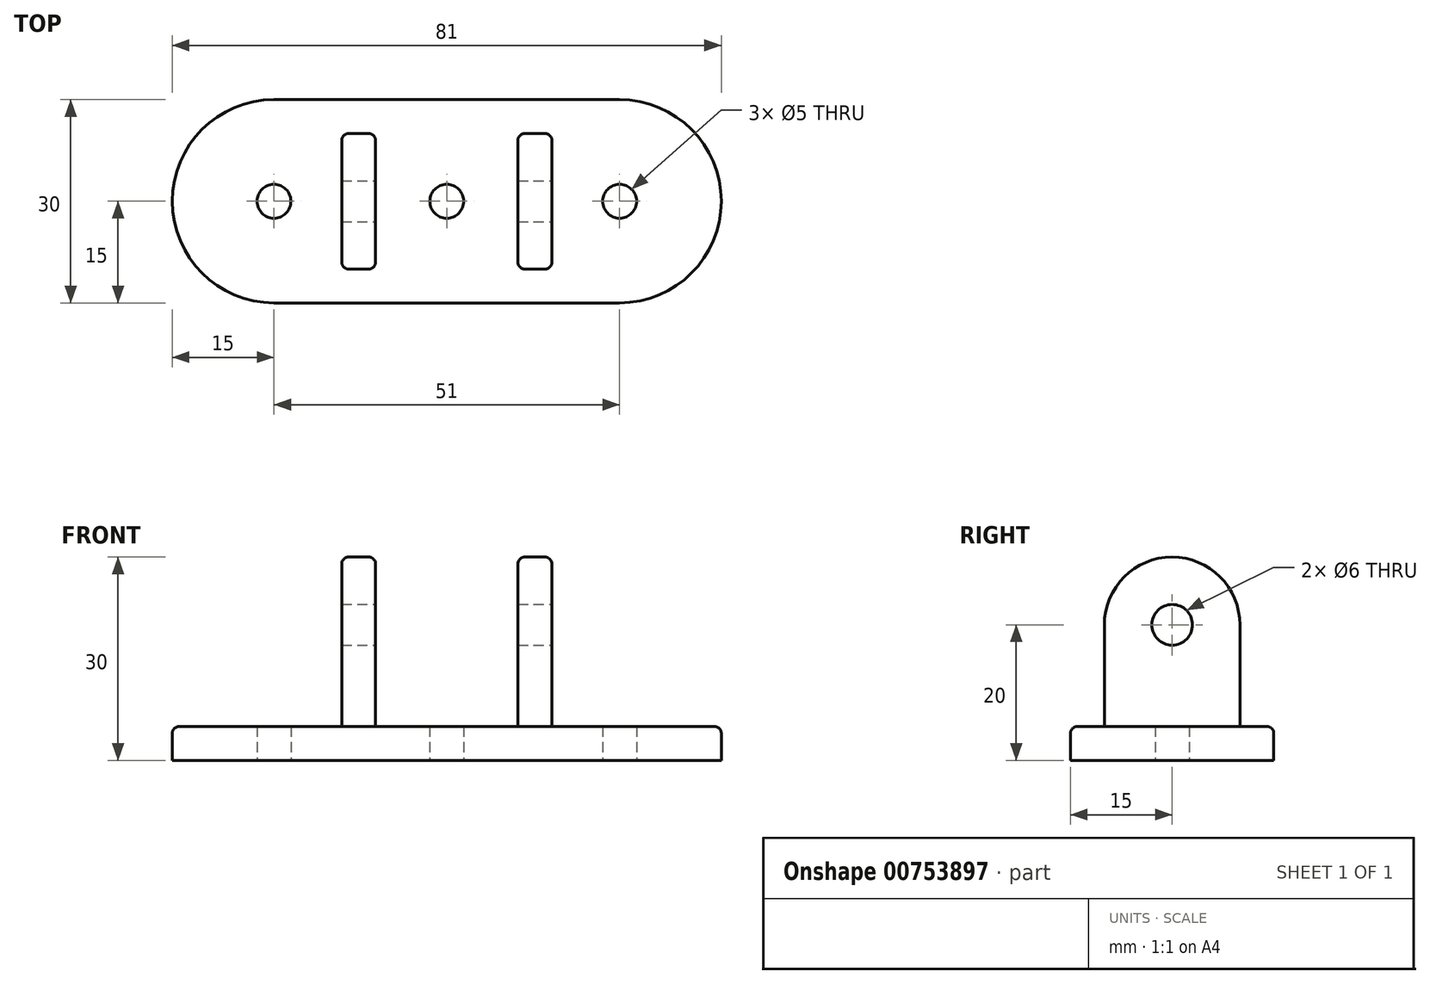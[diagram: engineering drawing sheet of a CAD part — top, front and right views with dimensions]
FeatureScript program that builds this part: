
annotation { "Feature Type Name" : "Feature", "Feature Type Description" : "" }
export const myFeature = defineFeature(function(context is Context, id is Id, definition is map)
    precondition{}
    {
        {
            var Q0;
            Q0=qCreatedBy(makeId("Top.planeOp"),FACE);
            var sketch = newSketch(context, id + "F0", { "sketchPlane" : qUnion([Q0])});
            skLineSegment(sketch, "E0", {"start": v(-0.06, 23.44) * mm, "end": v(-0.06, -19.85) * mm, "construction": true});
            skLineSegment(sketch, "E1.bottom", {"start": v(-25.5, -15) * mm, "end": v(25.5, -15) * mm});
            skLineSegment(sketch, "E1.top", {"start": v(-25.5, 15) * mm, "end": v(25.5, 15) * mm});
            skLineSegment(sketch, "E1.left", {"start": v(-25.5, -15) * mm, "end": v(-25.5, 15) * mm});
            skLineSegment(sketch, "E1.right", {"start": v(25.5, -15) * mm, "end": v(25.5, 15) * mm});
            skPoint(sketch, "E1.middle", {"position": v(0, 0) * mm});
            skCircle(sketch, "E2", {"center": v(-25.5, 0) * mm, "radius": 15 * mm});
            skCircle(sketch, "E3", {"center": v(25.5, 0) * mm, "radius": 15 * mm});
            skCircle(sketch, "E4", {"center": v(-25.5, 0) * mm, "radius": 2.5 * mm});
            skCircle(sketch, "E5", {"center": v(25.5, 0) * mm, "radius": 2.5 * mm});
            skCircle(sketch, "E6", {"center": v(0, 0) * mm, "radius": 2.5 * mm});
            skSolve(sketch);
        }
        {
            var Q0;
            Q0 = qSketchRegion(id + "F0", true);
            extrude(context, id + "F1", {"entities" : qUnion([Q0]), "depth" : 5 * mm, "offsetDistance" : 25 * mm});
        }
        {
            var Q0;
            Q0=makeQuery(id+"F1.opExtrude","CAP_FACE",FACE,{"disambiguationData":[OSD([sQuery(id+"F0.wireOp",EDGE,"E1.bottom"),sQuery(id+"F0.wireOp",EDGE,"E1.top"),sQuery(id+"F0.wireOp",EDGE,"E2"),sQuery(id+"F0.wireOp",EDGE,"E3"),sQuery(id+"F0.wireOp",EDGE,"khoQNaXH-vrLh-hDA5-w1uk-dnxeg6mnAbA2"),sQuery(id+"F0.wireOp",EDGE,"SrZ0nGfz-5AU4-rjPK-6jrb-PTzUXWZE5eXR")])],"isStart":false});
            var sketch = newSketch(context, id + "F2", { "sketchPlane" : qUnion([Q0])});
            skLineSegment(sketch, "E7.bottom", {"start": v(-10.5, -10) * mm, "end": v(-15.5, -10) * mm});
            skLineSegment(sketch, "E7.top", {"start": v(-10.5, 10) * mm, "end": v(-15.5, 10) * mm});
            skLineSegment(sketch, "E7.left", {"start": v(-10.5, -10) * mm, "end": v(-10.5, 10) * mm});
            skLineSegment(sketch, "E7.right", {"start": v(-15.5, -10) * mm, "end": v(-15.5, 10) * mm});
            skPoint(sketch, "E7.middle", {"position": v(-13, 0) * mm});
            skLineSegment(sketch, "E8.bottom", {"start": v(15.5, -10) * mm, "end": v(10.5, -10) * mm});
            skLineSegment(sketch, "E8.top", {"start": v(15.5, 10) * mm, "end": v(10.5, 10) * mm});
            skLineSegment(sketch, "E8.left", {"start": v(15.5, -10) * mm, "end": v(15.5, 10) * mm});
            skLineSegment(sketch, "E8.right", {"start": v(10.5, -10) * mm, "end": v(10.5, 10) * mm});
            skPoint(sketch, "E8.middle", {"position": v(13, 0) * mm});
            skSolve(sketch);
        }
        {
            var Q0;
            Q0=makeQuery(id+"F2.imprint","IMPRINT",FACE,{"disambiguationData":[TD([[makeQuery(id+"F2.imprint","IMPRINT",EDGE,{"derivedFrom":sQuery(id+"F2.wireOp",EDGE,"E8.bottom")}),-1.0]])]});
            extrude(context, id + "F3", {"entities" : qUnion([Q0]), "operationType" : NewBodyOperationType.ADD, "depth" : 15 * mm, "offsetDistance" : 25 * mm});
        }
        {
            var Q0;
            Q0=makeQuery(id+"F2.imprint","IMPRINT",FACE,{"disambiguationData":[TD([[makeQuery(id+"F2.imprint","IMPRINT",EDGE,{"derivedFrom":sQuery(id+"F2.wireOp",EDGE,"E7.bottom")}),-1.0]])]});
            extrude(context, id + "F4", {"entities" : qUnion([Q0]), "operationType" : NewBodyOperationType.ADD, "depth" : 15 * mm, "offsetDistance" : 25 * mm});
        }
        {
            var Q0;
            Q0=makeQuery(id+"F4.opExtrude","SWEPT_FACE",FACE,{"disambiguationData":[OSD([sQuery(id+"F2.wireOp",EDGE,"E7.left")])]});
            var sketch = newSketch(context, id + "F5", { "sketchPlane" : qUnion([Q0])});
            skCircle(sketch, "E9", {"center": v(0, 20) * mm, "radius": 10 * mm});
            skCircle(sketch, "E10", {"center": v(0, 20) * mm, "radius": 3 * mm});
            skSolve(sketch);
        }
        {
            var Q0;
            Q0 = qSketchRegion(id + "F5", true);
            extrude(context, id + "F6", {"entities" : qUnion([Q0]), "operationType" : NewBodyOperationType.ADD, "depth" : -5 * mm, "offsetDistance" : 25 * mm});
        }
        {
            var Q0;
            {var subQ0=sQuery(id+"F5.wireOp",EDGE,"E10");var subQ1=makeQuery(id+"F4.opExtrude","CAP_EDGE",EDGE,{"disambiguationData":[OSD([sQuery(id+"F2.wireOp",EDGE,"E7.left")])],"isStart":false});var subQ2=makeQuery(id+"F5.imprint","INTERSECT",VERTEX,{"disambiguationData":[OD(0.0)],"derivedFrom":[subQ1,subQ0]});Q0=makeQuery(id+"F5.imprint","IMPRINT",FACE,{"disambiguationData":[TD([[makeQuery(id+"F5.imprint","IMPRINT",EDGE,{"disambiguationData":[TD([[subQ2,-1.0]])],"derivedFrom":subQ0}),1.0]])]});}
            extrude(context, id + "F7", {"entities" : qUnion([Q0]), "operationType" : NewBodyOperationType.REMOVE, "oppositeDirection" : true, "depth" : 5 * mm, "offsetDistance" : 25 * mm});
        }
        {
            var Q0;
            Q0=makeQuery(id+"F3.opExtrude","SWEPT_FACE",FACE,{"disambiguationData":[OSD([sQuery(id+"F2.wireOp",EDGE,"E8.left")])]});
            var sketch = newSketch(context, id + "F8", { "sketchPlane" : qUnion([Q0])});
            skCircle(sketch, "E11", {"center": v(0, 20) * mm, "radius": 10 * mm});
            skCircle(sketch, "E12", {"center": v(0, 20) * mm, "radius": 3 * mm});
            skSolve(sketch);
        }
        {
            var Q0;
            Q0 = qSketchRegion(id + "F8", true);
            extrude(context, id + "F9", {"entities" : qUnion([Q0]), "operationType" : NewBodyOperationType.ADD, "depth" : -5 * mm, "offsetDistance" : 25 * mm});
        }
        {
            var Q0;
            {var subQ0=sQuery(id+"F8.wireOp",EDGE,"E12");var subQ1=makeQuery(id+"F3.opExtrude","CAP_EDGE",EDGE,{"disambiguationData":[OSD([sQuery(id+"F2.wireOp",EDGE,"E8.left")])],"isStart":false});var subQ2=makeQuery(id+"F8.imprint","INTERSECT",VERTEX,{"disambiguationData":[OD(0.0)],"derivedFrom":[subQ1,subQ0]});Q0=makeQuery(id+"F8.imprint","IMPRINT",FACE,{"disambiguationData":[TD([[makeQuery(id+"F8.imprint","IMPRINT",EDGE,{"disambiguationData":[TD([[subQ2,-1.0]])],"derivedFrom":subQ0}),1.0]])]});}
            extrude(context, id + "F10", {"entities" : qUnion([Q0]), "operationType" : NewBodyOperationType.REMOVE, "depth" : -5 * mm, "offsetDistance" : 25 * mm});
        }
        {
            var Q0;
            Q0=makeQuery(id+"F4.opExtrude","SWEPT_EDGE",EDGE,{"disambiguationData":[OSD([sQuery(id+"F2.wireOp",EDGE,"E7.bottom"),sQuery(id+"F2.wireOp",EDGE,"E7.left")])]});
            var Q1;
            Q1=makeQuery(id+"F3.opExtrude","SWEPT_EDGE",EDGE,{"disambiguationData":[OSD([sQuery(id+"F2.wireOp",EDGE,"E8.bottom"),sQuery(id+"F2.wireOp",EDGE,"E8.left")])]});
            var Q2;
            Q2=makeQuery(id+"F4.opExtrude","SWEPT_EDGE",EDGE,{"disambiguationData":[OSD([sQuery(id+"F2.wireOp",EDGE,"E7.bottom"),sQuery(id+"F2.wireOp",EDGE,"E7.right")])]});
            var Q3;
            Q3=makeQuery(id+"F3.opExtrude","SWEPT_EDGE",EDGE,{"disambiguationData":[OSD([sQuery(id+"F2.wireOp",EDGE,"E8.bottom"),sQuery(id+"F2.wireOp",EDGE,"E8.right")])]});
            fillet(context, id + "F11", {"entities" : qUnion([Q0, Q1, Q2, Q3]), "radius" : 1 * mm, "tangentPropagation" : true, "allowEdgeOverflow" : false});
        }
        {
            var Q0;
            Q0=makeQuery(id+"F1.opExtrude","CAP_EDGE",EDGE,{"disambiguationData":[OSD([sQuery(id+"F0.wireOp",EDGE,"E1.bottom")])],"isStart":false});
            fillet(context, id + "F12", {"entities" : qUnion([Q0]), "radius" : 1 * mm, "tangentPropagation" : true, "allowEdgeOverflow" : false});
        }
    });
